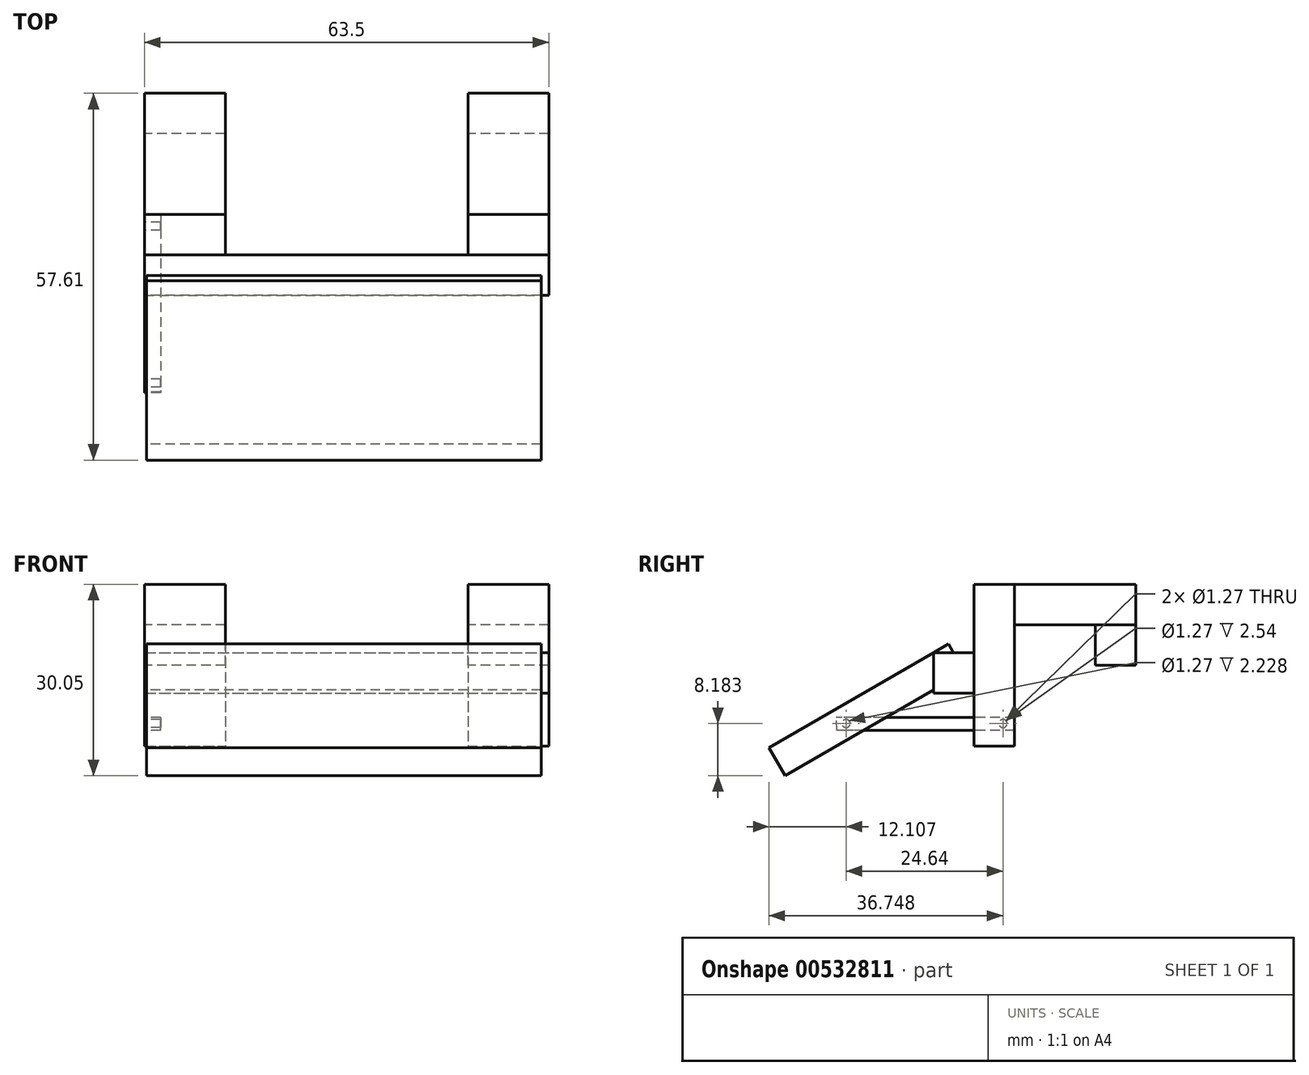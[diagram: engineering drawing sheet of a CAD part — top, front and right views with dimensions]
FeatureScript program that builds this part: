
annotation { "Feature Type Name" : "Feature", "Feature Type Description" : "" }
export const myFeature = defineFeature(function(context is Context, id is Id, definition is map)
    precondition{}
    {
        {
            var Q0;
            Q0=qCreatedBy(makeId("Front.planeOp"),FACE);
            var sketch = newSketch(context, id + "F0", { "sketchPlane" : qUnion([Q0])});
            skLineSegment(sketch, "E0.bottom", {"start": v(-31.75, 19.22) * mm, "end": v(-19.05, 19.22) * mm});
            skLineSegment(sketch, "E0.top", {"start": v(-31.75, -6.18) * mm, "end": v(-19.05, -6.18) * mm});
            skLineSegment(sketch, "E0.left", {"start": v(-31.75, 19.22) * mm, "end": v(-31.75, -6.18) * mm});
            skLineSegment(sketch, "E0.right", {"start": v(-19.05, 19.22) * mm, "end": v(-19.05, -6.18) * mm});
            skLineSegment(sketch, "E1.bottom", {"start": v(19.05, 19.22) * mm, "end": v(31.75, 19.22) * mm});
            skLineSegment(sketch, "E1.top", {"start": v(19.05, -6.18) * mm, "end": v(31.75, -6.18) * mm});
            skLineSegment(sketch, "E1.left", {"start": v(19.05, 19.22) * mm, "end": v(19.05, -6.18) * mm});
            skLineSegment(sketch, "E1.right", {"start": v(31.75, 19.22) * mm, "end": v(31.75, -6.18) * mm});
            skSolve(sketch);
        }
        {
            var Q0;
            Q0=makeQuery(id+"F0.imprint","IMPRINT",FACE,{"disambiguationData":[TD([[makeQuery(id+"F0.imprint","IMPRINT",EDGE,{"derivedFrom":sQuery(id+"F0.wireOp",EDGE,"E0.bottom")}),-1.0]])]});
            var Q1;
            Q1=makeQuery(id+"F0.imprint","IMPRINT",FACE,{"disambiguationData":[TD([[makeQuery(id+"F0.imprint","IMPRINT",EDGE,{"derivedFrom":sQuery(id+"F0.wireOp",EDGE,"E1.bottom")}),-1.0]])]});
            extrude(context, id + "F1", {"entities" : qUnion([Q0, Q1]), "depth" : 6.35 * mm, "offsetDistance" : 25.4 * mm});
        }
        {
            var Q0;
            Q0=makeQuery(id+"F1.opExtrude","CAP_FACE",FACE,{"disambiguationData":[OSD([sQuery(id+"F0.wireOp",EDGE,"E1.bottom"),sQuery(id+"F0.wireOp",EDGE,"E1.top"),sQuery(id+"F0.wireOp",EDGE,"E1.left"),sQuery(id+"F0.wireOp",EDGE,"E1.right")])],"isStart":true});
            var sketch = newSketch(context, id + "F2", { "sketchPlane" : qUnion([Q0])});
            skLineSegment(sketch, "E2.bottom", {"start": v(-31.75, 19.22) * mm, "end": v(-19.05, 19.22) * mm});
            skLineSegment(sketch, "E2.top", {"start": v(-31.75, 12.87) * mm, "end": v(-19.05, 12.87) * mm});
            skLineSegment(sketch, "E2.left", {"start": v(-31.75, 19.22) * mm, "end": v(-31.75, 12.87) * mm});
            skLineSegment(sketch, "E2.right", {"start": v(-19.05, 19.22) * mm, "end": v(-19.05, 12.87) * mm});
            skSolve(sketch);
        }
        {
            var Q0;
            Q0=makeQuery(id+"F1.opExtrude","CAP_FACE",FACE,{"disambiguationData":[OSD([sQuery(id+"F0.wireOp",EDGE,"E0.bottom"),sQuery(id+"F0.wireOp",EDGE,"E0.top"),sQuery(id+"F0.wireOp",EDGE,"E0.left"),sQuery(id+"F0.wireOp",EDGE,"E0.right")])],"isStart":true});
            var sketch = newSketch(context, id + "F3", { "sketchPlane" : qUnion([Q0])});
            skLineSegment(sketch, "E3.bottom", {"start": v(19.05, 19.22) * mm, "end": v(31.75, 19.22) * mm});
            skLineSegment(sketch, "E3.top", {"start": v(19.05, 12.87) * mm, "end": v(31.75, 12.87) * mm});
            skLineSegment(sketch, "E3.left", {"start": v(19.05, 19.22) * mm, "end": v(19.05, 12.87) * mm});
            skLineSegment(sketch, "E3.right", {"start": v(31.75, 19.22) * mm, "end": v(31.75, 12.87) * mm});
            skSolve(sketch);
        }
        {
            var Q0;
            Q0=makeQuery(id+"F2.imprint","IMPRINT",FACE,{"disambiguationData":[TD([[makeQuery(id+"F2.imprint","IMPRINT",EDGE,{"derivedFrom":sQuery(id+"F2.wireOp",EDGE,"E2.bottom")}),1.0]])]});
            var Q1;
            Q1=makeQuery(id+"F3.imprint","IMPRINT",FACE,{"disambiguationData":[TD([[makeQuery(id+"F3.imprint","IMPRINT",EDGE,{"derivedFrom":sQuery(id+"F3.wireOp",EDGE,"E3.bottom")}),1.0]])]});
            extrude(context, id + "F4", {"entities" : qUnion([Q0, Q1]), "depth" : 19.05 * mm, "offsetDistance" : 25.4 * mm});
        }
        {
            var Q0;
            Q0=makeQuery(id+"F4.opExtrude","SWEPT_FACE",FACE,{"disambiguationData":[OSD([sQuery(id+"F2.wireOp",EDGE,"E2.top")])]});
            var sketch = newSketch(context, id + "F5", { "sketchPlane" : qUnion([Q0])});
            skLineSegment(sketch, "E4.bottom", {"start": v(31.75, -19.05) * mm, "end": v(19.05, -19.05) * mm});
            skLineSegment(sketch, "E4.top", {"start": v(31.75, -12.7) * mm, "end": v(19.05, -12.7) * mm});
            skLineSegment(sketch, "E4.left", {"start": v(31.75, -19.05) * mm, "end": v(31.75, -12.7) * mm});
            skLineSegment(sketch, "E4.right", {"start": v(19.05, -19.05) * mm, "end": v(19.05, -12.7) * mm});
            skSolve(sketch);
        }
        {
            var Q0;
            Q0=makeQuery(id+"F4.opExtrude","SWEPT_FACE",FACE,{"disambiguationData":[OSD([sQuery(id+"F3.wireOp",EDGE,"E3.top")])]});
            var sketch = newSketch(context, id + "F6", { "sketchPlane" : qUnion([Q0])});
            skLineSegment(sketch, "E5.bottom", {"start": v(-19.05, -19.05) * mm, "end": v(-31.75, -19.05) * mm});
            skLineSegment(sketch, "E5.top", {"start": v(-19.05, -12.7) * mm, "end": v(-31.75, -12.7) * mm});
            skLineSegment(sketch, "E5.left", {"start": v(-19.05, -19.05) * mm, "end": v(-19.05, -12.7) * mm});
            skLineSegment(sketch, "E5.right", {"start": v(-31.75, -19.05) * mm, "end": v(-31.75, -12.7) * mm});
            skSolve(sketch);
        }
        {
            var Q0;
            Q0=makeQuery(id+"F5.imprint","IMPRINT",FACE,{"disambiguationData":[TD([[makeQuery(id+"F5.imprint","IMPRINT",EDGE,{"derivedFrom":sQuery(id+"F5.wireOp",EDGE,"E4.bottom")}),-1.0]])]});
            var Q1;
            Q1=makeQuery(id+"F6.imprint","IMPRINT",FACE,{"disambiguationData":[TD([[makeQuery(id+"F6.imprint","IMPRINT",EDGE,{"derivedFrom":sQuery(id+"F6.wireOp",EDGE,"E5.bottom")}),-1.0]])]});
            extrude(context, id + "F7", {"entities" : qUnion([Q0, Q1]), "depth" : 6.35 * mm, "offsetDistance" : 25.4 * mm});
        }
        {
            var Q0;
            Q0=makeQuery(id+"F1.opExtrude","CAP_FACE",FACE,{"disambiguationData":[OSD([sQuery(id+"F0.wireOp",EDGE,"E0.bottom"),sQuery(id+"F0.wireOp",EDGE,"E0.top"),sQuery(id+"F0.wireOp",EDGE,"E0.left"),sQuery(id+"F0.wireOp",EDGE,"E0.right")])],"isStart":false});
            var sketch = newSketch(context, id + "F8", { "sketchPlane" : qUnion([Q0])});
            skLineSegment(sketch, "E6.bottom", {"start": v(-31.75, 8.5) * mm, "end": v(31.75, 8.5) * mm});
            skLineSegment(sketch, "E6.top", {"start": v(-31.75, 2.15) * mm, "end": v(31.75, 2.15) * mm});
            skLineSegment(sketch, "E6.left", {"start": v(-31.75, 8.5) * mm, "end": v(-31.75, 2.15) * mm});
            skLineSegment(sketch, "E6.right", {"start": v(31.75, 8.5) * mm, "end": v(31.75, 2.15) * mm});
            skSolve(sketch);
        }
        {
            var Q0;
            {var subQ0=sQuery(id+"F8.wireOp",EDGE,"E6.right");Q0=makeQuery(id+"F8.imprint","IMPRINT",FACE,{"disambiguationData":[TD([[makeQuery(id+"F8.imprint","IMPRINT",EDGE,{"derivedFrom":subQ0}),-1.0]])]});}
            var Q1;
            {var subQ0=sQuery(id+"F8.wireOp",EDGE,"E6.left");Q1=makeQuery(id+"F8.imprint","IMPRINT",FACE,{"disambiguationData":[TD([[makeQuery(id+"F8.imprint","IMPRINT",EDGE,{"derivedFrom":subQ0}),1.0]])]});}
            extrude(context, id + "F9", {"entities" : qUnion([Q0, Q1]), "depth" : 6.35 * mm, "offsetDistance" : 25.4 * mm});
        }
        {
            var Q0;
            Q0=makeQuery(id+"F9.opExtrude","CAP_EDGE",EDGE,{"disambiguationData":[OSD([sQuery(id+"F8.wireOp",EDGE,"E6.bottom")])],"isStart":false});
            cPlane(context, id + "F10", {"entities" : qUnion([Q0]), "cplaneType" : CPlaneType.LINE_ANGLE, "offset" : 25.4 * mm, "angle" : 120 * degree, "width" : 152.4 * mm, "height" : 152.4 * mm});
        }
        {
            var Q0;
            Q0=qCreatedBy(id+"F10.planeOp",FACE);
            var sketch = newSketch(context, id + "F11", { "sketchPlane" : qUnion([Q0])});
            skLineSegment(sketch, "E7", {"start": v(-31.44, -4.05) * mm, "end": v(30.55, -4.05) * mm});
            skLineSegment(sketch, "E8", {"start": v(30.55, -4.05) * mm, "end": v(30.55, -36.61) * mm});
            skLineSegment(sketch, "E9", {"start": v(30.55, -36.61) * mm, "end": v(-31.44, -36.61) * mm});
            skLineSegment(sketch, "E10", {"start": v(-31.44, -4.05) * mm, "end": v(-31.44, -36.61) * mm});
            skSolve(sketch);
        }
        {
            var Q0;
            Q0=makeQuery(id+"F11.imprint","IMPRINT",FACE,{"disambiguationData":[TD([[makeQuery(id+"F11.imprint","IMPRINT",EDGE,{"derivedFrom":sQuery(id+"F11.wireOp",EDGE,"E7")}),-1.0]])]});
            extrude(context, id + "F12", {"entities" : qUnion([Q0]), "operationType" : NewBodyOperationType.ADD, "oppositeDirection" : true, "depth" : 5.08 * mm, "offsetDistance" : 25.4 * mm});
        }
        {
            var Q0;
            Q0=makeQuery(id+"F1.opExtrude","SWEPT_FACE",FACE,{"disambiguationData":[OSD([sQuery(id+"F0.wireOp",EDGE,"E0.left")])]});
            var sketch = newSketch(context, id + "F13", { "sketchPlane" : qUnion([Q0])});
            skLineSegment(sketch, "E11", {"start": v(0, -1.68) * mm, "end": v(28, -1.69) * mm});
            skLineSegment(sketch, "E12", {"start": v(0, -3.72) * mm, "end": v(27.87, -3.72) * mm});
            skLineSegment(sketch, "E13", {"start": v(27.87, -3.72) * mm, "end": v(28, -1.69) * mm});
            skLineSegment(sketch, "E14", {"start": v(0, -1.68) * mm, "end": v(0, -3.72) * mm});
            skSolve(sketch);
        }
        {
            var Q0;
            {var subQ0=sQuery(id+"F13.wireOp",EDGE,"E13");Q0=makeQuery(id+"F13.imprint","IMPRINT",FACE,{"disambiguationData":[TD([[makeQuery(id+"F13.imprint","IMPRINT",EDGE,{"derivedFrom":subQ0}),1.0]])]});}
            var Q1;
            {var subQ0=sQuery(id+"F13.wireOp",EDGE,"E14");Q1=makeQuery(id+"F13.imprint","IMPRINT",FACE,{"disambiguationData":[TD([[makeQuery(id+"F13.imprint","IMPRINT",EDGE,{"derivedFrom":subQ0}),1.0]])]});}
            extrude(context, id + "F14", {"entities" : qUnion([Q0, Q1]), "oppositeDirection" : true, "depth" : 2.54 * mm, "offsetDistance" : 25.4 * mm});
        }
        {
            var Q0;
            Q0=makeQuery(id+"F14.opExtrude","CAP_FACE",FACE,{"disambiguationData":[OSD([sQuery(id+"F13.wireOp",EDGE,"E11"),sQuery(id+"F13.wireOp",EDGE,"E12"),sQuery(id+"F13.wireOp",EDGE,"E13"),sQuery(id+"F13.wireOp",EDGE,"E14")])],"isStart":true});
            var sketch = newSketch(context, id + "F15", { "sketchPlane" : qUnion([Q0])});
            skCircle(sketch, "E15", {"center": v(1.81, -2.65) * mm, "radius": 0.64 * mm});
            skCircle(sketch, "E16", {"center": v(26.45, -2.65) * mm, "radius": 0.64 * mm});
            skSolve(sketch);
        }
        {
            var Q0;
            Q0=makeQuery(id+"F15.imprint","IMPRINT",FACE,{"disambiguationData":[TD([[makeQuery(id+"F15.imprint","IMPRINT",EDGE,{"derivedFrom":sQuery(id+"F15.wireOp",EDGE,"E15")}),1.0]])]});
            var Q1;
            Q1=makeQuery(id+"F15.imprint","IMPRINT",FACE,{"disambiguationData":[TD([[makeQuery(id+"F15.imprint","IMPRINT",EDGE,{"derivedFrom":sQuery(id+"F15.wireOp",EDGE,"E16")}),1.0]])]});
            extrude(context, id + "F16", {"entities" : qUnion([Q0, Q1]), "operationType" : NewBodyOperationType.REMOVE, "oppositeDirection" : true, "depth" : 2.54 * mm, "offsetDistance" : 25.4 * mm});
        }
    });
